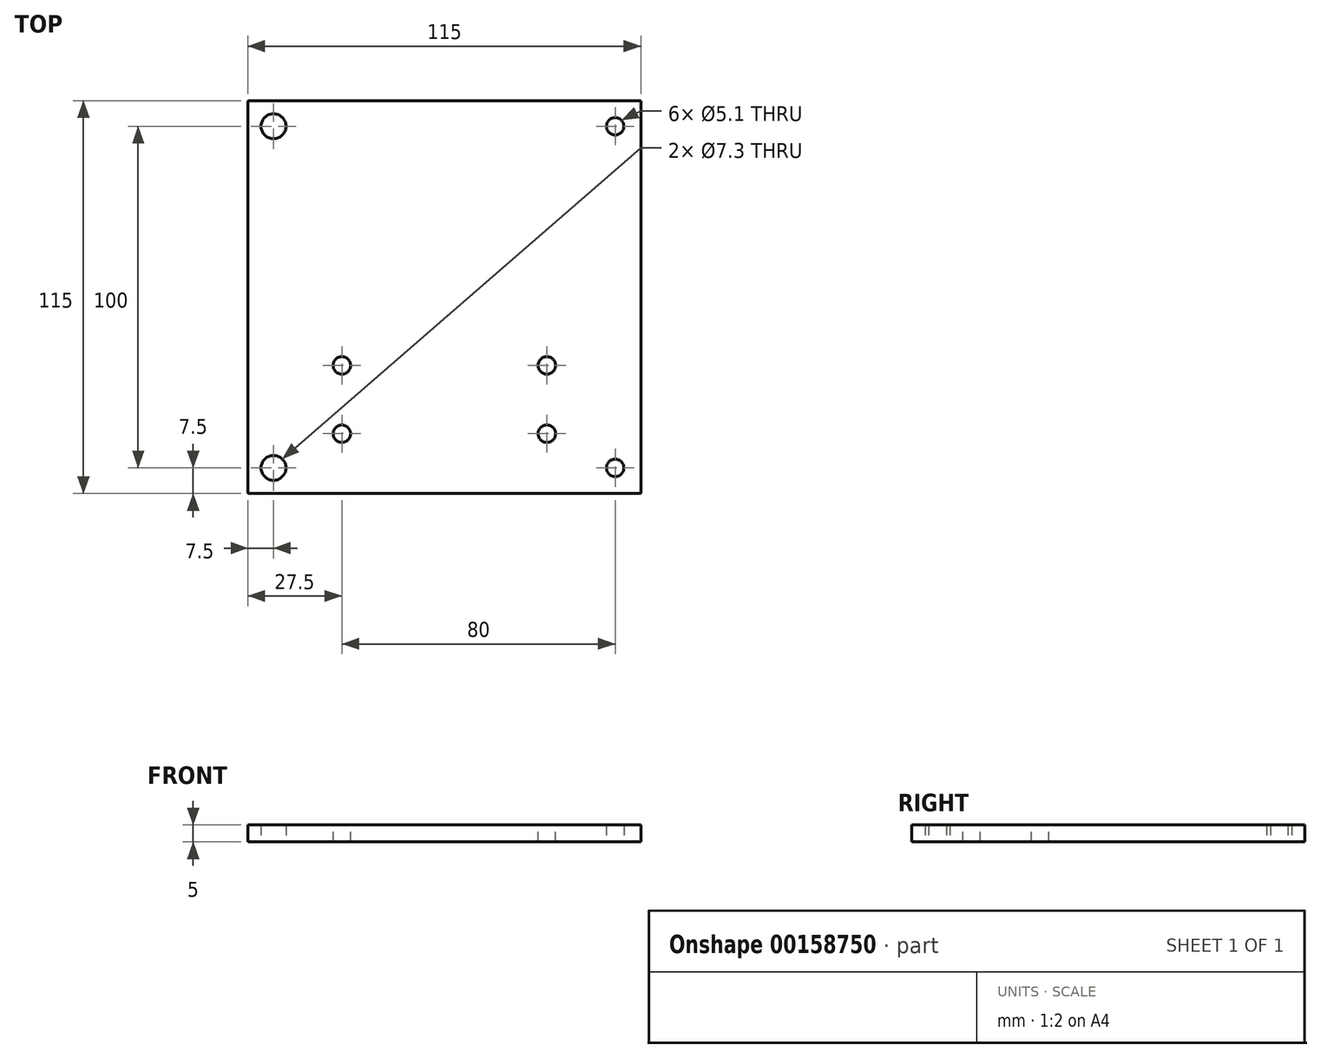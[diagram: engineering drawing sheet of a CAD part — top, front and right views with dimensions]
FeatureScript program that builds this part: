
annotation { "Feature Type Name" : "Feature", "Feature Type Description" : "" }
export const myFeature = defineFeature(function(context is Context, id is Id, definition is map)
    precondition{}
    {
        {
            var Q0;
            Q0=qCreatedBy(makeId("Top.planeOp"),FACE);
            var sketch = newSketch(context, id + "F1", { "sketchPlane" : qUnion([Q0])});
            skLineSegment(sketch, "E0.bottom", {"start": v(50, -50) * mm, "end": v(-50, -50) * mm});
            skLineSegment(sketch, "E0.top", {"start": v(50, 50) * mm, "end": v(-50, 50) * mm});
            skLineSegment(sketch, "E0.left", {"start": v(50, -50) * mm, "end": v(50, 50) * mm});
            skLineSegment(sketch, "E0.right", {"start": v(-50, -50) * mm, "end": v(-50, 50) * mm});
            skPoint(sketch, "E0.middle", {"position": v(0, 0) * mm});
            skLineSegment(sketch, "E1.bottom", {"start": v(57.5, -57.5) * mm, "end": v(-57.5, -57.5) * mm});
            skLineSegment(sketch, "E1.top", {"start": v(57.5, 57.5) * mm, "end": v(-57.5, 57.5) * mm});
            skLineSegment(sketch, "E1.left", {"start": v(57.5, -57.5) * mm, "end": v(57.5, 57.5) * mm});
            skLineSegment(sketch, "E1.right", {"start": v(-57.5, -57.5) * mm, "end": v(-57.5, 57.5) * mm});
            skSolve(sketch);
        }
        {
            var Q0;
            Q0=makeQuery(id+"F1.imprint","IMPRINT",FACE,{"disambiguationData":[TD([[makeQuery(id+"F1.imprint","IMPRINT",EDGE,{"derivedFrom":sQuery(id+"F1.wireOp",EDGE,"E0.bottom")}),-1.0]])]});
            var Q1;
            Q1=makeQuery(id+"F1.imprint","IMPRINT",FACE,{"disambiguationData":[TD([[makeQuery(id+"F1.imprint","IMPRINT",EDGE,{"derivedFrom":sQuery(id+"F1.wireOp",EDGE,"E0.bottom")}),1.0]])]});
            extrude(context, id + "F2", {"entities" : qUnion([Q0, Q1]), "depth" : 5 * mm});
        }
        {
            var Q0;
            Q0=sQuery(id+"F1.wireOp",VERTEX,"E0.left.start");
            var Q1;
            Q1=sQuery(id+"F1.wireOp",VERTEX,"E0.left.end");
            var Q2;
            Q2=makeQuery(id+"F2.opExtrude","SWEPT_BODY",BODY,{"disambiguationData":[OSD([sQuery(id+"F1.wireOp",EDGE,"E1.bottom"),sQuery(id+"F1.wireOp",EDGE,"E1.top"),sQuery(id+"F1.wireOp",EDGE,"E1.left"),sQuery(id+"F1.wireOp",EDGE,"E1.right")])]});
            hole(context, id + "F3", {"style" : HoleStyle.SIMPLE, "endStyle" : HoleEndStyle.THROUGH, "oppositeDirection" : true, "holeDiameter" : 5.1 * mm, "locations" : qUnion([Q0, Q1]), "scope" : qUnion([Q2]), "isTappedThrough" : true});
        }
        {
            var Q0;
            Q0=sQuery(id+"F1.wireOp",VERTEX,"E0.right.end");
            var Q1;
            Q1=sQuery(id+"F1.wireOp",VERTEX,"E0.bottom.end");
            var Q2;
            Q2=makeQuery(id+"F2.opExtrude","SWEPT_BODY",BODY,{"disambiguationData":[OSD([sQuery(id+"F1.wireOp",EDGE,"E1.bottom"),sQuery(id+"F1.wireOp",EDGE,"E1.top"),sQuery(id+"F1.wireOp",EDGE,"E1.left"),sQuery(id+"F1.wireOp",EDGE,"E1.right")])]});
            hole(context, id + "F0", {"style" : HoleStyle.SIMPLE, "endStyle" : HoleEndStyle.THROUGH, "oppositeDirection" : true, "holeDiameter" : 7.3 * mm, "locations" : qUnion([Q0, Q1]), "scope" : qUnion([Q2]), "isTappedThrough" : true});
        }
        {
            var Q0;
            Q0=makeQuery(id+"F2.opExtrude","CAP_FACE",FACE,{"disambiguationData":[OSD([sQuery(id+"F1.wireOp",EDGE,"E1.bottom"),sQuery(id+"F1.wireOp",EDGE,"E1.top"),sQuery(id+"F1.wireOp",EDGE,"E1.left"),sQuery(id+"F1.wireOp",EDGE,"E1.right")])],"isStart":false});
            var sketch = newSketch(context, id + "F4", { "sketchPlane" : qUnion([Q0])});
            skPoint(sketch, "E2", {"position": v(30, -40) * mm});
            skPoint(sketch, "E3", {"position": v(-30, -40) * mm});
            skPoint(sketch, "E4", {"position": v(30, -20) * mm});
            skPoint(sketch, "E5", {"position": v(-30, -20) * mm});
            skSolve(sketch);
        }
        {
            var Q0;
            Q0=sQuery(id+"F4.wireOp",VERTEX,"E4");
            var Q1;
            Q1=sQuery(id+"F4.wireOp",VERTEX,"E2");
            var Q2;
            Q2=sQuery(id+"F4.wireOp",VERTEX,"E5");
            var Q3;
            Q3=sQuery(id+"F4.wireOp",VERTEX,"E3");
            var Q4;
            Q4=makeQuery(id+"F2.opExtrude","SWEPT_BODY",BODY,{"disambiguationData":[OSD([sQuery(id+"F1.wireOp",EDGE,"E1.bottom"),sQuery(id+"F1.wireOp",EDGE,"E1.top"),sQuery(id+"F1.wireOp",EDGE,"E1.left"),sQuery(id+"F1.wireOp",EDGE,"E1.right")])]});
            hole(context, id + "F5", {"style" : HoleStyle.SIMPLE, "endStyle" : HoleEndStyle.THROUGH, "holeDiameter" : 5.1 * mm, "locations" : qUnion([Q0, Q1, Q2, Q3]), "scope" : qUnion([Q4]), "isTappedThrough" : true});
        }
    });
